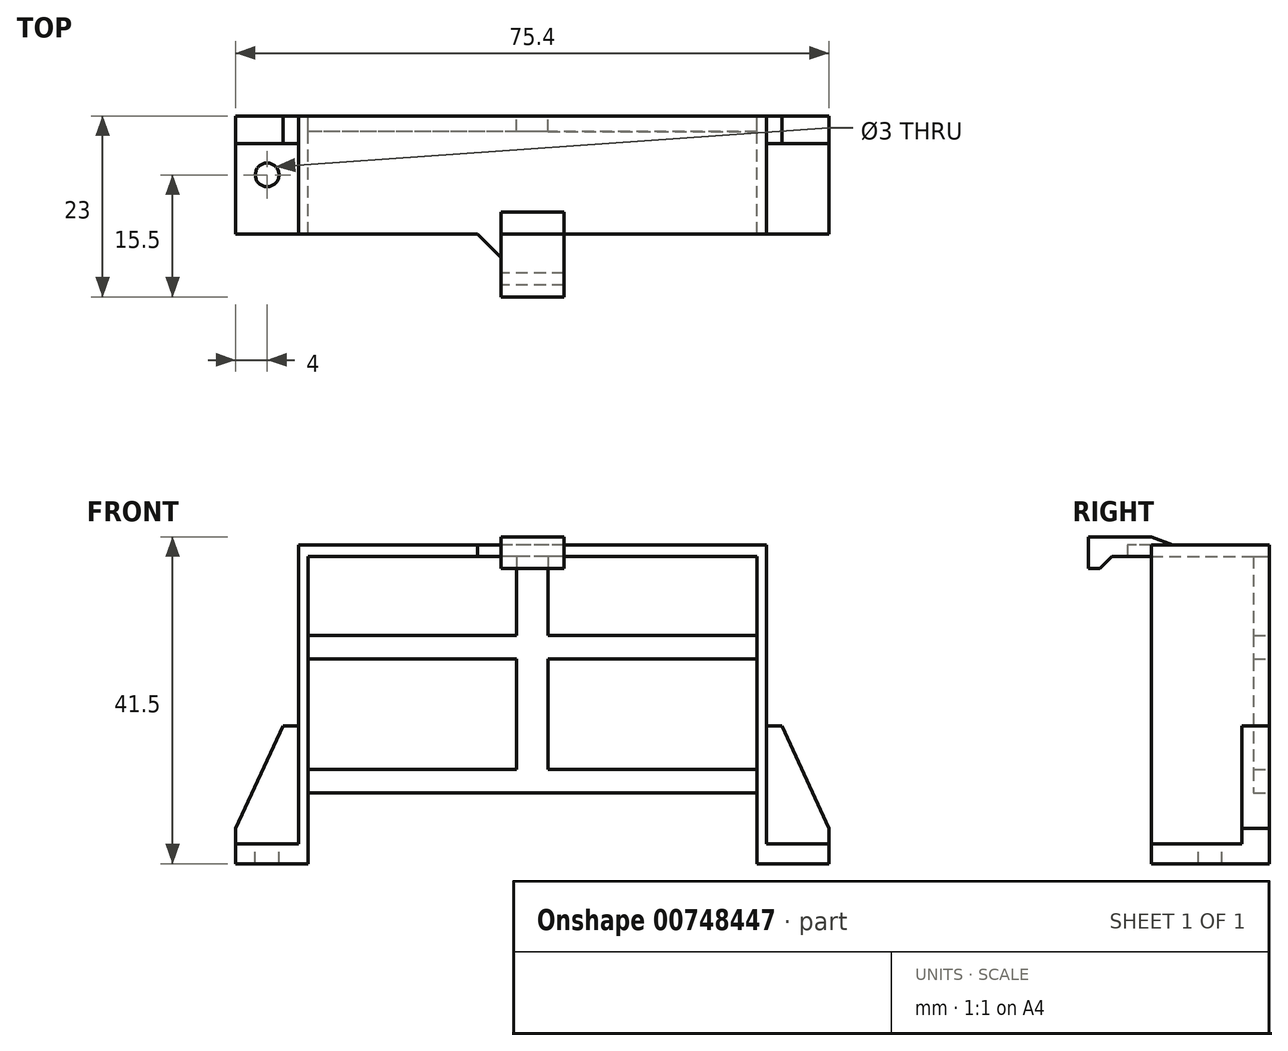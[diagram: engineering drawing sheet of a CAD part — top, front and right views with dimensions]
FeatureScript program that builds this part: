
annotation { "Feature Type Name" : "Feature", "Feature Type Description" : "" }
export const myFeature = defineFeature(function(context is Context, id is Id, definition is map)
    precondition{}
    {
        {
            var Q0;
            Q0=qCreatedBy(makeId("Front.planeOp"),FACE);
            var sketch = newSketch(context, id + "F0", { "sketchPlane" : qUnion([Q0])});
            skLineSegment(sketch, "E0", {"start": v(0, 38) * mm, "end": v(28.5, 38) * mm});
            skLineSegment(sketch, "E1", {"start": v(28.5, 38) * mm, "end": v(28.5, 0) * mm});
            skLineSegment(sketch, "E2", {"start": v(28.5, 0) * mm, "end": v(37.7, 0) * mm});
            skLineSegment(sketch, "E3", {"start": v(37.7, 0) * mm, "end": v(37.7, 1.5) * mm});
            skLineSegment(sketch, "E4", {"start": v(37.7, 1.5) * mm, "end": v(29.7, 1.5) * mm});
            skLineSegment(sketch, "E5", {"start": v(29.7, 1.5) * mm, "end": v(29.7, 39.5) * mm});
            skLineSegment(sketch, "E6", {"start": v(29.7, 39.5) * mm, "end": v(0, 39.5) * mm});
            skLineSegment(sketch, "E7", {"start": v(0, 39.5) * mm, "end": v(0, 38) * mm, "construction": true});
            skLineSegment(sketch, "E8.MirrorCS", {"start": v(-29.7, 39.5) * mm, "end": v(0, 39.5) * mm});
            skLineSegment(sketch, "E9.MirrorCS", {"start": v(0, 38) * mm, "end": v(-28.5, 38) * mm});
            skLineSegment(sketch, "E10.MirrorCS", {"start": v(-29.7, 1.5) * mm, "end": v(-29.7, 39.5) * mm});
            skLineSegment(sketch, "E11.MirrorCS", {"start": v(-28.5, 38) * mm, "end": v(-28.5, 0) * mm});
            skLineSegment(sketch, "E12.MirrorCS", {"start": v(-28.5, 0) * mm, "end": v(-37.7, 0) * mm});
            skLineSegment(sketch, "E13.MirrorCS", {"start": v(-37.7, 1.5) * mm, "end": v(-29.7, 1.5) * mm});
            skLineSegment(sketch, "E14.MirrorCS", {"start": v(-37.7, 0) * mm, "end": v(-37.7, 1.5) * mm});
            skSolve(sketch);
        }
        {
            var Q0;
            Q0=makeQuery(id+"F0.imprint","IMPRINT",FACE,{"disambiguationData":[TD([[makeQuery(id+"F0.imprint","IMPRINT",EDGE,{"derivedFrom":sQuery(id+"F0.wireOp",EDGE,"E0")}),1.0]])]});
            extrude(context, id + "F1", {"entities" : qUnion([Q0]), "depth" : 15 * mm, "offsetDistance" : 25 * mm});
        }
        {
            var Q0;
            Q0=makeQuery(id+"F1.opExtrude","CAP_FACE",FACE,{"disambiguationData":[OSD([sQuery(id+"F0.wireOp",EDGE,"E0"),sQuery(id+"F0.wireOp",EDGE,"E1"),sQuery(id+"F0.wireOp",EDGE,"E2"),sQuery(id+"F0.wireOp",EDGE,"E3"),sQuery(id+"F0.wireOp",EDGE,"E4"),sQuery(id+"F0.wireOp",EDGE,"E5"),sQuery(id+"F0.wireOp",EDGE,"E6"),sQuery(id+"F0.wireOp",EDGE,"E8.MirrorCS"),sQuery(id+"F0.wireOp",EDGE,"E9.MirrorCS"),sQuery(id+"F0.wireOp",EDGE,"E10.MirrorCS"),sQuery(id+"F0.wireOp",EDGE,"E11.MirrorCS"),sQuery(id+"F0.wireOp",EDGE,"E12.MirrorCS"),sQuery(id+"F0.wireOp",EDGE,"E13.MirrorCS"),sQuery(id+"F0.wireOp",EDGE,"E14.MirrorCS")])],"isStart":true});
            var sketch = newSketch(context, id + "F2", { "sketchPlane" : qUnion([Q0])});
            skLineSegment(sketch, "E15.bottom", {"start": v(-28.5, 8) * mm, "end": v(28.5, 8) * mm});
            skLineSegment(sketch, "E15.top", {"start": v(-28.5, 11) * mm, "end": v(-2, 11) * mm});
            skLineSegment(sketch, "E15.left", {"start": v(-28.5, 8) * mm, "end": v(-28.5, 11) * mm});
            skLineSegment(sketch, "E15.right", {"start": v(28.5, 8) * mm, "end": v(28.5, 11) * mm});
            skLineSegment(sketch, "E16.bottom", {"start": v(28.5, 25) * mm, "end": v(2, 25) * mm});
            skLineSegment(sketch, "E16.top", {"start": v(28.5, 28) * mm, "end": v(2, 28) * mm});
            skLineSegment(sketch, "E16.left", {"start": v(28.5, 25) * mm, "end": v(28.5, 28) * mm});
            skLineSegment(sketch, "E16.right", {"start": v(-28.5, 25) * mm, "end": v(-28.5, 28) * mm});
            skLineSegment(sketch, "E17.bottom", {"start": v(-2, 38) * mm, "end": v(2, 38) * mm});
            skLineSegment(sketch, "E17.top", {"start": v(-2, 8) * mm, "end": v(2, 8) * mm});
            skLineSegment(sketch, "E17.left", {"start": v(-2, 38) * mm, "end": v(-2, 28) * mm});
            skLineSegment(sketch, "E17.right", {"start": v(2, 38) * mm, "end": v(2, 28) * mm});
            skLineSegment(sketch, "E18.trimOffspring", {"start": v(-2, 28) * mm, "end": v(-28.5, 28) * mm});
            skLineSegment(sketch, "E19.trimOffspring", {"start": v(-2, 25) * mm, "end": v(-28.5, 25) * mm});
            skLineSegment(sketch, "E20.trimOffspring", {"start": v(-2, 25) * mm, "end": v(-2, 11) * mm});
            skLineSegment(sketch, "E21.trimOffspring", {"start": v(2, 25) * mm, "end": v(2, 11) * mm});
            skLineSegment(sketch, "E22.trimOffspring", {"start": v(2, 11) * mm, "end": v(28.5, 11) * mm});
            skSolve(sketch);
        }
        {
            var Q0;
            Q0=makeQuery(id+"F2.imprint","IMPRINT",FACE,{"disambiguationData":[TD([[makeQuery(id+"F2.imprint","IMPRINT",EDGE,{"derivedFrom":sQuery(id+"F2.wireOp",EDGE,"E15.top")}),-1.0]])]});
            extrude(context, id + "F3", {"entities" : qUnion([Q0]), "operationType" : NewBodyOperationType.ADD, "oppositeDirection" : true, "depth" : 2 * mm, "offsetDistance" : 25 * mm});
        }
        {
            var Q0;
            Q0=makeQuery(id+"F1.opExtrude","SWEPT_FACE",FACE,{"disambiguationData":[OSD([sQuery(id+"F0.wireOp",EDGE,"E13.MirrorCS")])]});
            var sketch = newSketch(context, id + "F4", { "sketchPlane" : qUnion([Q0])});
            skLineSegment(sketch, "E23", {"start": v(-37.7, 0) * mm, "end": v(-29.7, -15) * mm, "construction": true});
            skCircle(sketch, "E24", {"center": v(-33.7, -7.5) * mm, "radius": 1.5 * mm});
            skLineSegment(sketch, "E25", {"start": v(0, 0) * mm, "end": v(0, -15.18) * mm, "construction": true});
            skCircle(sketch, "E26.MirrorC", {"center": v(33.7, -7.5) * mm, "radius": 1.5 * mm});
            skSolve(sketch);
        }
        {
            var Q0;
            Q0=makeQuery(id+"F4.imprint","IMPRINT",FACE,{"disambiguationData":[TD([[makeQuery(id+"F4.imprint","IMPRINT",EDGE,{"derivedFrom":sQuery(id+"F4.wireOp",EDGE,"E24")}),1.0]])]});
            var Q1;
            Q1=makeQuery(id+"F4.imprint","IMPRINT",FACE,{"disambiguationData":[TD([[makeQuery(id+"F4.imprint","IMPRINT",EDGE,{"derivedFrom":sQuery(id+"F4.wireOp",EDGE,"E26.MirrorC")}),-1.0]])]});
            extrude(context, id + "F5", {"entities" : qUnion([Q0, Q1]), "operationType" : NewBodyOperationType.REMOVE, "oppositeDirection" : true, "depth" : 25 * mm, "offsetDistance" : 25 * mm});
        }
        {
            var Q0;
            Q0=qCreatedBy(makeId("Right.planeOp"),FACE);
            var sketch = newSketch(context, id + "F6", { "sketchPlane" : qUnion([Q0])});
            skLineSegment(sketch, "E27.0", {"start": v(-2, 25) * mm, "end": v(-2, 11) * mm, "construction": true});
            skLineSegment(sketch, "E28.0", {"start": v(-15, 38) * mm, "end": v(-15, 0) * mm, "construction": true});
            skLineSegment(sketch, "E29.0", {"start": v(-15, 1.5) * mm, "end": v(-15, 39.5) * mm, "construction": true});
            skLineSegment(sketch, "E30.bottom", {"start": v(-15, 40.5) * mm, "end": v(-23, 40.5) * mm});
            skLineSegment(sketch, "E30.top", {"start": v(-15, 38) * mm, "end": v(-20, 38) * mm});
            skLineSegment(sketch, "E30.left", {"start": v(-15, 39.5) * mm, "end": v(-15, 38) * mm});
            skLineSegment(sketch, "E30.right", {"start": v(-23, 40.5) * mm, "end": v(-23, 38) * mm});
            skLineSegment(sketch, "E31", {"start": v(-23, 38) * mm, "end": v(-23, 36.5) * mm});
            skLineSegment(sketch, "E32", {"start": v(-23, 36.5) * mm, "end": v(-21.5, 36.5) * mm});
            skLineSegment(sketch, "E33", {"start": v(-21.5, 36.5) * mm, "end": v(-20, 38) * mm});
            skLineSegment(sketch, "E34", {"start": v(-15, 40.5) * mm, "end": v(-12.25, 39.5) * mm});
            skLineSegment(sketch, "E35", {"start": v(-12.25, 39.5) * mm, "end": v(-15, 39.5) * mm});
            skSolve(sketch);
        }
        {
            var Q0;
            Q0=makeQuery(id+"F6.imprint","IMPRINT",FACE,{"disambiguationData":[TD([[makeQuery(id+"F6.imprint","IMPRINT",EDGE,{"derivedFrom":sQuery(id+"F6.wireOp",EDGE,"E30.bottom")}),1.0]])]});
            extrude(context, id + "F7", {"entities" : qUnion([Q0]), "operationType" : NewBodyOperationType.ADD, "endBound" : BoundingType.SYMMETRIC, "depth" : 8 * mm, "offsetDistance" : 25 * mm});
        }
        {
            var Q0;
            Q0=makeQuery(id+"F7.opExtrude","CAP_EDGE",EDGE,{"disambiguationData":[OSD([sQuery(id+"F6.wireOp",EDGE,"E30.left")])],"isStart":false});
            var Q1;
            Q1=makeQuery(id+"F7.opExtrude","CAP_EDGE",EDGE,{"disambiguationData":[OSD([sQuery(id+"F6.wireOp",EDGE,"E30.left")])],"isStart":true});
            chamfer(context, id + "F8", {"entities" : qUnion([Q0, Q1]), "width" : 3 * mm, "tangentPropagation" : true});
        }
        {
            var Q0;
            Q0=makeQuery(id+"F3.boolean.opBoolean","MERGE",FACE,{"derivedFrom":[makeQuery(id+"F1.opExtrude","CAP_FACE",FACE,{"disambiguationData":[OSD([sQuery(id+"F0.wireOp",EDGE,"E0"),sQuery(id+"F0.wireOp",EDGE,"E1"),sQuery(id+"F0.wireOp",EDGE,"E2"),sQuery(id+"F0.wireOp",EDGE,"E3"),sQuery(id+"F0.wireOp",EDGE,"E4"),sQuery(id+"F0.wireOp",EDGE,"E5"),sQuery(id+"F0.wireOp",EDGE,"E6"),sQuery(id+"F0.wireOp",EDGE,"E8.MirrorCS"),sQuery(id+"F0.wireOp",EDGE,"E9.MirrorCS"),sQuery(id+"F0.wireOp",EDGE,"E10.MirrorCS"),sQuery(id+"F0.wireOp",EDGE,"E11.MirrorCS"),sQuery(id+"F0.wireOp",EDGE,"E12.MirrorCS"),sQuery(id+"F0.wireOp",EDGE,"E13.MirrorCS"),sQuery(id+"F0.wireOp",EDGE,"E14.MirrorCS")])],"isStart":true}),makeQuery(id+"F3.opExtrude","CAP_FACE",FACE,{"disambiguationData":[OSD([sQuery(id+"F2.wireOp",EDGE,"E15.bottom"),sQuery(id+"F2.wireOp",EDGE,"E15.top"),sQuery(id+"F2.wireOp",EDGE,"E15.left"),sQuery(id+"F2.wireOp",EDGE,"E15.right"),sQuery(id+"F2.wireOp",EDGE,"E16.bottom"),sQuery(id+"F2.wireOp",EDGE,"E16.top"),sQuery(id+"F2.wireOp",EDGE,"E16.left"),sQuery(id+"F2.wireOp",EDGE,"E16.right"),sQuery(id+"F2.wireOp",EDGE,"E17.bottom"),sQuery(id+"F2.wireOp",EDGE,"E17.top"),sQuery(id+"F2.wireOp",EDGE,"E17.left"),sQuery(id+"F2.wireOp",EDGE,"E17.right"),sQuery(id+"F2.wireOp",EDGE,"E18.trimOffspring"),sQuery(id+"F2.wireOp",EDGE,"E19.trimOffspring"),sQuery(id+"F2.wireOp",EDGE,"E20.trimOffspring"),sQuery(id+"F2.wireOp",EDGE,"E21.trimOffspring"),sQuery(id+"F2.wireOp",EDGE,"E22.trimOffspring")])],"isStart":true})]});
            var sketch = newSketch(context, id + "F9", { "sketchPlane" : qUnion([Q0])});
            skLineSegment(sketch, "E36.0", {"start": v(37.7, 1.5) * mm, "end": v(29.7, 1.5) * mm});
            skLineSegment(sketch, "E37.0", {"start": v(29.7, 1.5) * mm, "end": v(29.7, 16.5) * mm});
            skLineSegment(sketch, "E38.0", {"start": v(-37.7, 1.5) * mm, "end": v(-29.7, 1.5) * mm});
            skLineSegment(sketch, "E39.0", {"start": v(-29.7, 1.5) * mm, "end": v(-29.7, 16.5) * mm});
            skLineSegment(sketch, "E40", {"start": v(37.7, 1.5) * mm, "end": v(37.7, 3.5) * mm});
            skLineSegment(sketch, "E41", {"start": v(37.7, 3.5) * mm, "end": v(31.7, 16.5) * mm});
            skPoint(sketch, "E42.orphan", {"position": v(29.7, 39.5) * mm});
            skLineSegment(sketch, "E43", {"start": v(-37.7, 1.5) * mm, "end": v(-37.7, 3.5) * mm});
            skLineSegment(sketch, "E44", {"start": v(-37.7, 3.5) * mm, "end": v(-31.7, 16.5) * mm});
            skPoint(sketch, "E45.orphan", {"position": v(-29.7, 39.5) * mm});
            skLineSegment(sketch, "E46", {"start": v(31.7, 16.5) * mm, "end": v(29.7, 16.5) * mm});
            skLineSegment(sketch, "E47", {"start": v(-29.7, 16.5) * mm, "end": v(-31.7, 16.5) * mm});
            skSolve(sketch);
        }
        {
            var Q0;
            Q0=makeQuery(id+"F9.imprint","IMPRINT",FACE,{"disambiguationData":[TD([[makeQuery(id+"F9.imprint","IMPRINT",EDGE,{"derivedFrom":sQuery(id+"F9.wireOp",EDGE,"E38.0")}),1.0]])]});
            var Q1;
            Q1=makeQuery(id+"F9.imprint","IMPRINT",FACE,{"disambiguationData":[TD([[makeQuery(id+"F9.imprint","IMPRINT",EDGE,{"derivedFrom":sQuery(id+"F9.wireOp",EDGE,"E36.0")}),-1.0]])]});
            extrude(context, id + "F10", {"entities" : qUnion([Q0, Q1]), "operationType" : NewBodyOperationType.ADD, "oppositeDirection" : true, "depth" : 3.5 * mm, "offsetDistance" : 25 * mm});
        }
        {
            var Q0;
            Q0=makeQuery(id+"F1.opExtrude","SWEPT_FACE",FACE,{"disambiguationData":[OSD([sQuery(id+"F0.wireOp",EDGE,"E12.MirrorCS")])]});
            var Q1;
            Q1=makeQuery(id+"F1.opExtrude","SWEPT_FACE",FACE,{"disambiguationData":[OSD([sQuery(id+"F0.wireOp",EDGE,"E2")])]});
            extrude(context, id + "F11", {"entities" : qUnion([Q0, Q1]), "operationType" : NewBodyOperationType.ADD, "depth" : 1 * mm, "offsetDistance" : 25 * mm});
        }
    });
